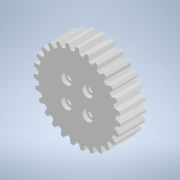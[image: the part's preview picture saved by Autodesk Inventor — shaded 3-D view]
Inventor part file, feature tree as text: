
AUTODESK INVENTOR PART (.ipt)
format: ipt  version: 2021 (Build 250183000, 183)  size: 232,448 bytes
history: native  units: mm
features: extrude x3, sketch x1, pattern_circular x1
ambient origin geometry x8: Origin, YZ Plane, XZ Plane, XY Plane, X Axis, Y Axis, Z Axis, Center Point
bodies: Solid1 (feature_tree)
feature tree (5):
  sketch  "Sketch1"  dims[d0=8.5mm d1=4.25mm d2=8.5mm d3=4.25mm d4=2.3mm d6=1.2mm d7=3.490659mm d8=2.0mm d9=1.5mm d10=4.2mm d11=1.0mm d12=0.0mm d13=2.5mm d14=0.0mm d15=2.5mm d16=0.0mm d17=270.0mm d18=360.0deg d20=28.0mm d21=8.0mm d22=0.0mm]
  extrude  "Extrusion1"  Depth=8.0mm
  extrude  "Extrusion2"  Depth=8.0mm
  extrude  "Extrusion3"  Depth=8.0mm
  pattern_circular  "Circular Pattern1"  [2 undecoded]
note: 2 required parameter values undecoded (feature->parameter linkage not recoverable at this tier; creation-order binding heuristic only, values carry confidence <= 0.55)
